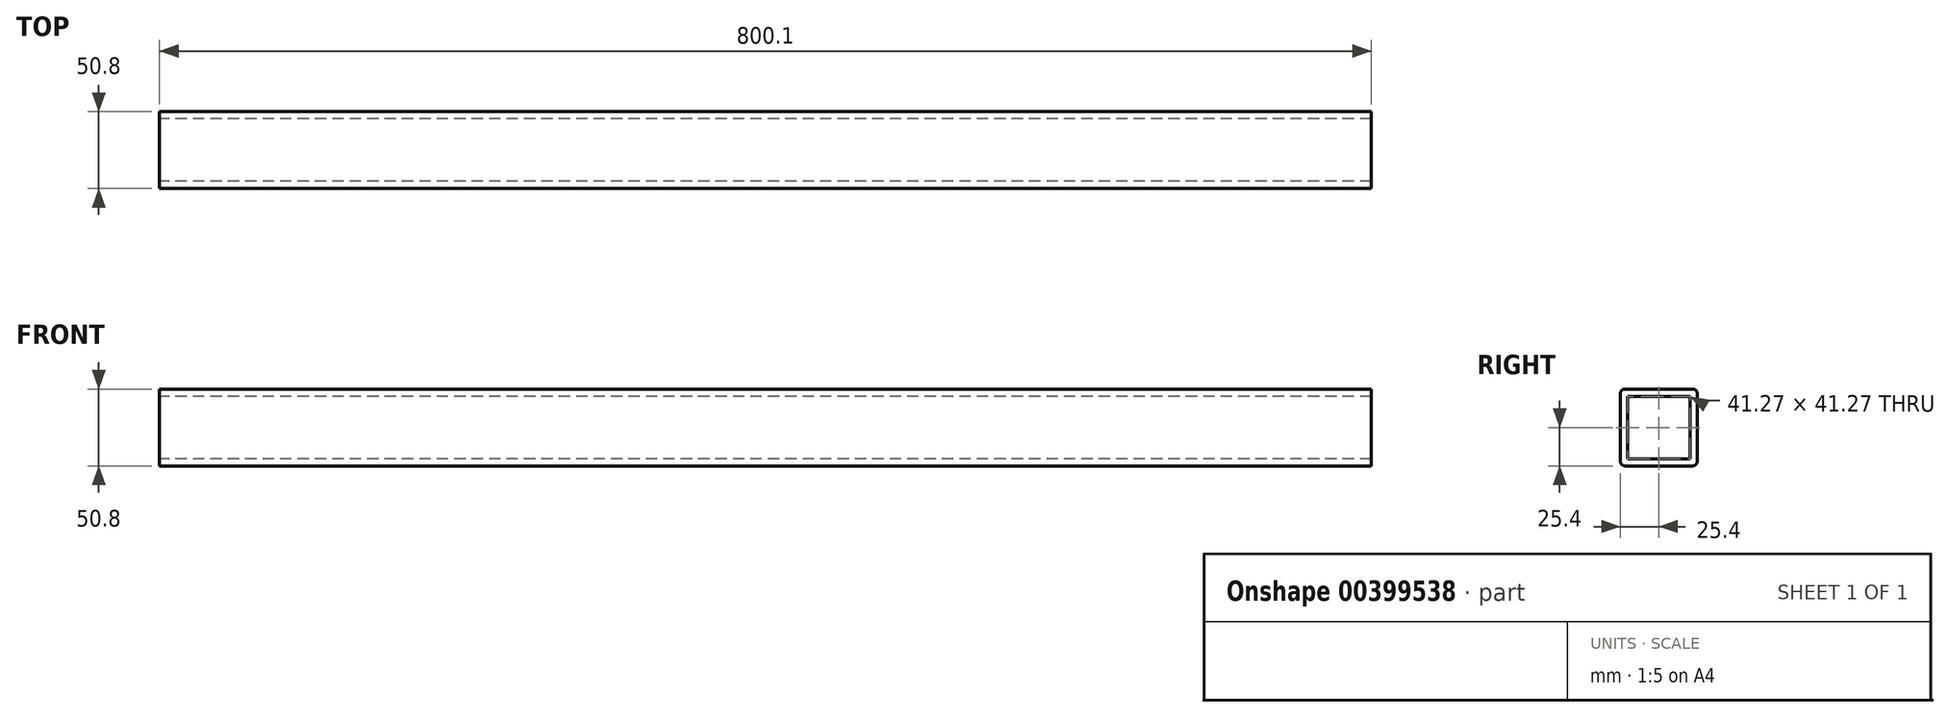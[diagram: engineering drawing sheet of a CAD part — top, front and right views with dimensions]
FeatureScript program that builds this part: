
annotation { "Feature Type Name" : "Feature", "Feature Type Description" : "" }
export const myFeature = defineFeature(function(context is Context, id is Id, definition is map)
    precondition{}
    {
        {
            var Q0;
            Q0=qCreatedBy(makeId("Right.planeOp"),FACE);
            var sketch = newSketch(context, id + "F0", { "sketchPlane" : qUnion([Q0])});
            skLineSegment(sketch, "E0.bottom", {"start": v(22.23, 25.4) * mm, "end": v(-22.23, 25.4) * mm});
            skLineSegment(sketch, "E0.top", {"start": v(22.23, -25.4) * mm, "end": v(-22.23, -25.4) * mm});
            skLineSegment(sketch, "E0.left", {"start": v(25.4, 22.23) * mm, "end": v(25.4, -22.23) * mm});
            skLineSegment(sketch, "E0.right", {"start": v(-25.4, 22.23) * mm, "end": v(-25.4, -22.23) * mm});
            skPoint(sketch, "E0.middle", {"position": v(0, 0) * mm});
            skPoint(sketch, "E1.visualSharp", {"position": v(-25.4, 25.4) * mm});
            skArc(sketch, "E1.filletArc", {"start": v(-22.23, 25.4) * mm, "mid": v(-24.47, 24.47) * mm, "end": v(-25.4, 22.23) * mm});
            skPoint(sketch, "E2.visualSharp", {"position": v(25.4, 25.4) * mm});
            skArc(sketch, "E2.filletArc", {"start": v(25.4, 22.23) * mm, "mid": v(24.47, 24.47) * mm, "end": v(22.23, 25.4) * mm});
            skPoint(sketch, "E3.visualSharp", {"position": v(25.4, -25.4) * mm});
            skArc(sketch, "E3.filletArc", {"start": v(22.23, -25.4) * mm, "mid": v(24.47, -24.47) * mm, "end": v(25.4, -22.23) * mm});
            skPoint(sketch, "E4.visualSharp", {"position": v(-25.4, -25.4) * mm});
            skArc(sketch, "E4.filletArc", {"start": v(-25.4, -22.23) * mm, "mid": v(-24.47, -24.47) * mm, "end": v(-22.23, -25.4) * mm});
            skLineSegment(sketch, "E5.0", {"start": v(-20.64, 20.64) * mm, "end": v(-20.64, -20.64) * mm});
            skLineSegment(sketch, "E5.1", {"start": v(20.64, 20.64) * mm, "end": v(-20.64, 20.64) * mm});
            skLineSegment(sketch, "E5.2", {"start": v(20.64, 20.64) * mm, "end": v(20.64, -20.64) * mm});
            skLineSegment(sketch, "E5.3", {"start": v(20.64, -20.64) * mm, "end": v(-20.64, -20.64) * mm});
            skSolve(sketch);
        }
        {
            var Q0;
            Q0=makeQuery(id+"F0.imprint","IMPRINT",FACE,{"disambiguationData":[TD([[makeQuery(id+"F0.imprint","IMPRINT",EDGE,{"derivedFrom":sQuery(id+"F0.wireOp",EDGE,"E0.bottom")}),1.0]])]});
            extrude(context, id + "F1", {"entities" : qUnion([Q0]), "endBound" : BoundingType.SYMMETRIC, "depth" : 800.1 * mm});
        }
    });
